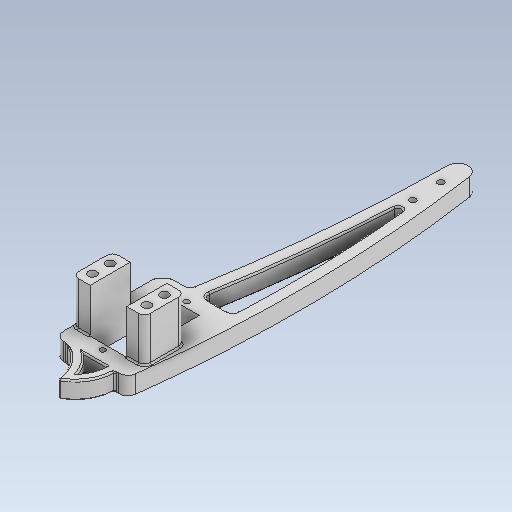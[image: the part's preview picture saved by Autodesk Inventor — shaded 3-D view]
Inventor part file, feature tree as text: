
AUTODESK INVENTOR PART (.ipt)
format: ipt  version: 2020.3 (Build 243373000, 373)  size: 375,808 bytes
history: native  units: mm
features: other x3, sketch x2
ambient origin geometry x8: Origin, YZ Plane, XZ Plane, XY Plane, X Axis, Y Axis, Z Axis, Center Point
bodies: Solid1 (feature_tree)
feature tree (5):
  other  "LegEnd_Right_v2.ipt"
  other  "Solid1::LegEnd_Right_v2.ipt"
  other  "TaggingFeature1"
  sketch  "Sketch1"  dims[d0=10.0mm]
  sketch  "Sketch3"
